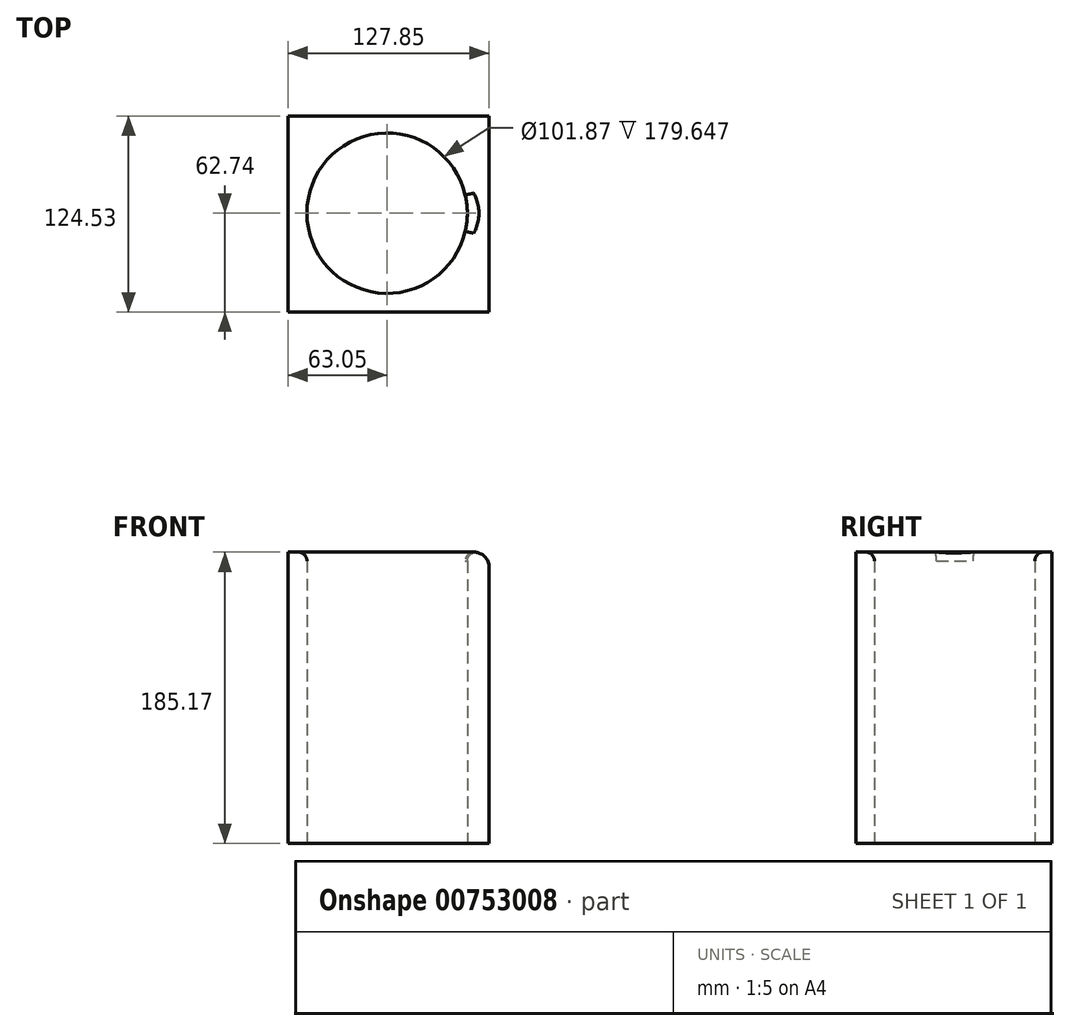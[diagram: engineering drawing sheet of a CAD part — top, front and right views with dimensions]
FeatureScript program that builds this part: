
annotation { "Feature Type Name" : "Feature", "Feature Type Description" : "" }
export const myFeature = defineFeature(function(context is Context, id is Id, definition is map)
    precondition{}
    {
        {
            var Q0;
            Q0=qCreatedBy(makeId("Top.planeOp"),FACE);
            var sketch = newSketch(context, id + "F0", { "sketchPlane" : qUnion([Q0])});
            skCircle(sketch, "E0", {"center": v(0, 0) * mm, "radius": 50.93 * mm});
            skLineSegment(sketch, "E1.bottom", {"start": v(-63.05, 61.8) * mm, "end": v(64.8, 61.8) * mm});
            skLineSegment(sketch, "E1.top", {"start": v(-63.05, -62.74) * mm, "end": v(64.8, -62.74) * mm});
            skLineSegment(sketch, "E1.left", {"start": v(-63.05, 61.8) * mm, "end": v(-63.05, -62.74) * mm});
            skLineSegment(sketch, "E1.right", {"start": v(64.8, 61.8) * mm, "end": v(64.8, -62.74) * mm});
            skSolve(sketch);
        }
        {
            var Q0;
            Q0=makeQuery(id+"F0.imprint","IMPRINT",FACE,{"disambiguationData":[TD([[makeQuery(id+"F0.imprint","IMPRINT",EDGE,{"derivedFrom":sQuery(id+"F0.wireOp",EDGE,"E0")}),-1.0]])]});
            extrude(context, id + "F1", {"entities" : qUnion([Q0]), "depth" : 185.17 * mm, "offsetDistance" : 25.4 * mm});
        }
        {
            var Q0;
            Q0=makeQuery(id+"F1.opExtrude","CAP_EDGE",EDGE,{"disambiguationData":[OSD([sQuery(id+"F0.wireOp",EDGE,"E1.right")])],"isStart":false});
            fillet(context, id + "F2", {"entities" : qUnion([Q0]), "radius" : 9.8 * mm, "tangentPropagation" : true, "allowEdgeOverflow" : false});
        }
        {
            var Q0;
            Q0=makeQuery(id+"F1.opExtrude","CAP_EDGE",EDGE,{"disambiguationData":[OSD([sQuery(id+"F0.wireOp",EDGE,"E0")])],"isStart":false});
            fillet(context, id + "F3", {"entities" : qUnion([Q0]), "radius" : 5.52 * mm, "tangentPropagation" : true, "allowEdgeOverflow" : false});
        }
    });
